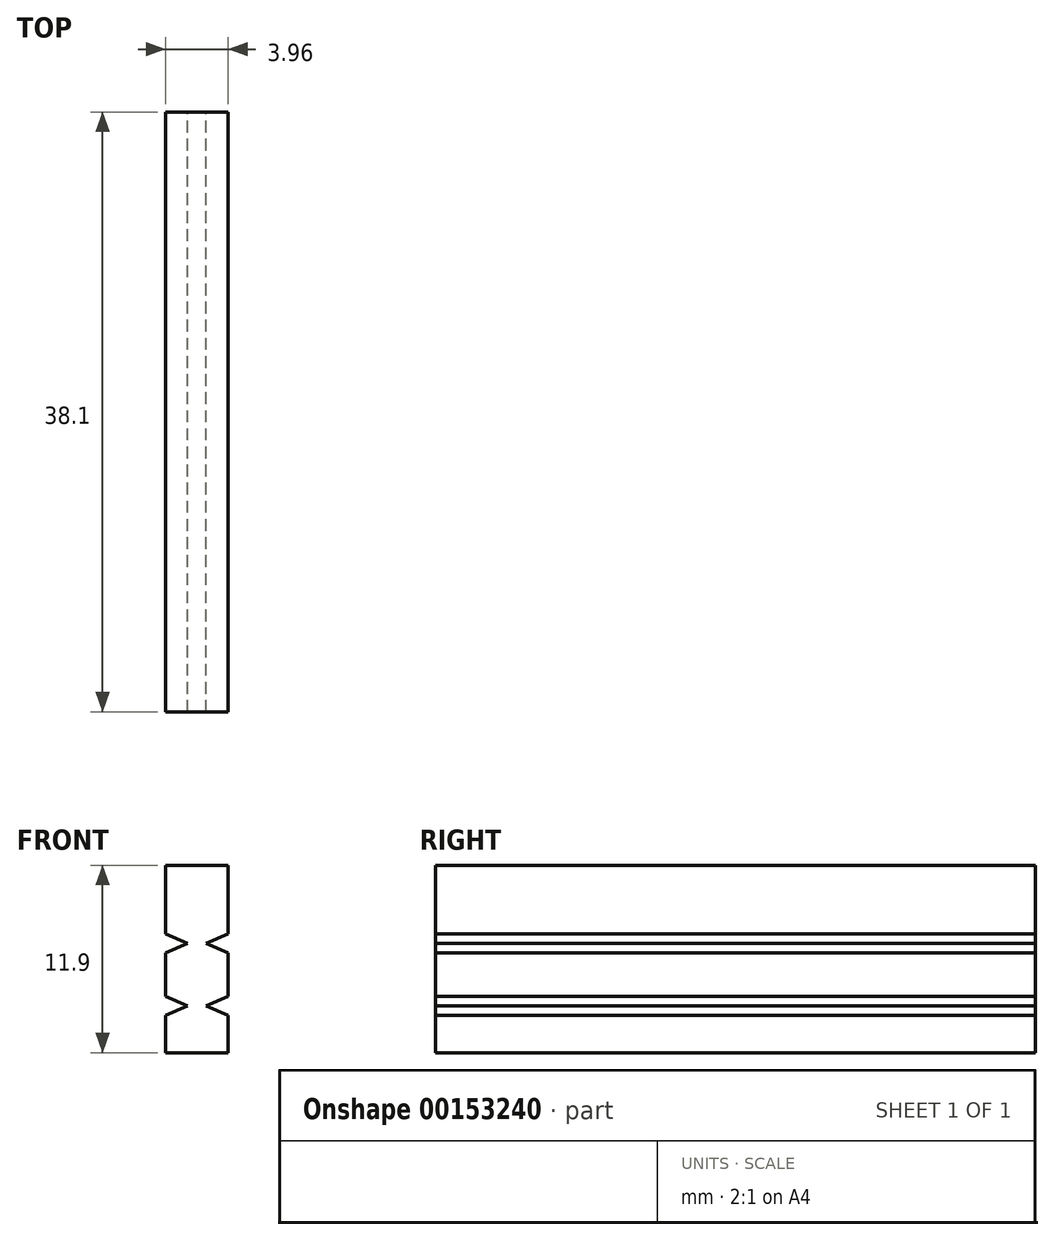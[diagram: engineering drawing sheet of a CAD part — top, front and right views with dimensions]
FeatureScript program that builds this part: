
annotation { "Feature Type Name" : "Feature", "Feature Type Description" : "" }
export const myFeature = defineFeature(function(context is Context, id is Id, definition is map)
    precondition{}
    {
        {
            var Q0;
            Q0=qCreatedBy(makeId("Front.planeOp"),FACE);
            var sketch = newSketch(context, id + "F0", { "sketchPlane" : qUnion([Q0])});
            skLineSegment(sketch, "E0.bottom", {"start": v(1.98, -5.95) * mm, "end": v(-1.98, -5.95) * mm});
            skLineSegment(sketch, "E0.top", {"start": v(1.98, 5.95) * mm, "end": v(-1.98, 5.95) * mm});
            skLineSegment(sketch, "E0.left", {"start": v(1.98, -5.95) * mm, "end": v(1.98, 5.95) * mm});
            skLineSegment(sketch, "E0.right", {"start": v(-1.98, -5.95) * mm, "end": v(-1.98, 5.95) * mm});
            skPoint(sketch, "E0.middle", {"position": v(0, 0) * mm});
            skLineSegment(sketch, "E1", {"start": v(-1.98, -2.38) * mm, "end": v(-0.6, -2.98) * mm});
            skLineSegment(sketch, "E2", {"start": v(-0.6, -2.98) * mm, "end": v(-1.98, -3.57) * mm});
            skLineSegment(sketch, "E3", {"start": v(0, 7.22) * mm, "end": v(0, -8.04) * mm, "construction": true});
            skLineSegment(sketch, "E4.MirrorCS", {"start": v(1.98, -2.38) * mm, "end": v(0.6, -2.98) * mm});
            skLineSegment(sketch, "E5.MirrorCS", {"start": v(0.6, -2.98) * mm, "end": v(1.98, -3.57) * mm});
            skLineSegment(sketch, "E6.0.1.0", {"start": v(-1.98, 1.59) * mm, "end": v(-0.6, 1) * mm});
            skLineSegment(sketch, "E6.0.1.1", {"start": v(-0.6, 1) * mm, "end": v(-1.98, 0.4) * mm});
            skLineSegment(sketch, "E6.0.1.2", {"start": v(1.98, 1.59) * mm, "end": v(0.6, 1) * mm});
            skLineSegment(sketch, "E6.0.1.3", {"start": v(0.6, 1) * mm, "end": v(1.98, 0.4) * mm});
            skLineSegment(sketch, "E6.direction1", {"start": v(-1.98, -2.38) * mm, "end": v(23.42, -2.38) * mm, "construction": true});
            skLineSegment(sketch, "E6.direction2", {"start": v(-1.98, -2.38) * mm, "end": v(-1.98, 1.59) * mm, "construction": true});
            skSolve(sketch);
        }
        {
            var Q0;
            {var subQ6=sQuery(id+"F0.wireOp",EDGE,"E0.bottom");Q0=makeQuery(id+"F0.imprint","IMPRINT",FACE,{"disambiguationData":[TD([[makeQuery(id+"F0.imprint","IMPRINT",EDGE,{"derivedFrom":subQ6}),-1.0]])]});}
            extrude(context, id + "F1", {"entities" : qUnion([Q0]), "depth" : 38.1 * mm});
        }
    });
